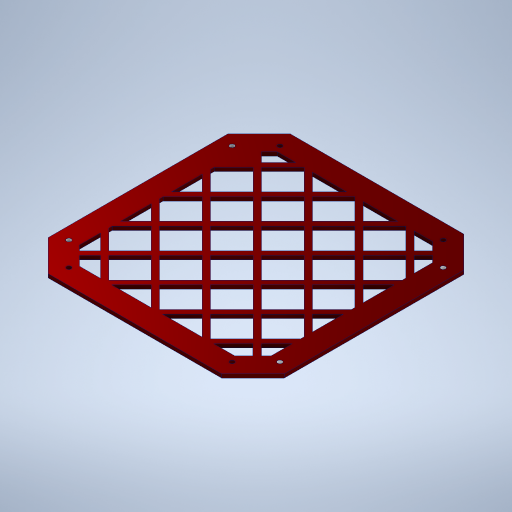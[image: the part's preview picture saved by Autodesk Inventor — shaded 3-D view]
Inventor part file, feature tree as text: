
AUTODESK INVENTOR PART (.ipt)
format: ipt  version: 2024.2 (Build 282272000, 272)  size: 547,328 bytes
history: native  units: in
note: dims shown in document units (in); Inventor stores cm internally (conversion verified against a paired STEP export)
features: extrude x4, sketch x4, chamfer x2, projected_geometry x2
ambient origin geometry x8: Origin, YZ Plane, XZ Plane, XY Plane, X Axis, Y Axis, Z Axis, Center Point
bodies: Body1 (feature_tree)
feature tree (12):
  extrude  "Extrusion4"  Depth=8.207in
  sketch  "Sketch5"  dims[d29=0.125in d30=0.0in d31=8.0in]
  extrude  "Extrusion7"  Depth=8.0in
  chamfer  "Chamfer1"  Distance=7.153in
  chamfer  "Chamfer2"  Distance=0.157in
  extrude  "Extrusion8"  Depth=1.25in
  extrude  "Extrusion9"  Depth=1.25in
  sketch  "Sketch4"  dims[d27=8.0in d28=8.207in]
  projected_geometry  "Projected Loop2"
  sketch  "Sketch8"  dims[d32=8.207in]
  projected_geometry  "Projected Loop5"
  sketch  "Sketch9"  dims[d33=5.533in d34=7.153in d39=0.157in d40=0.157in d41=0.157in d42=0.157in d43=1.0625in d44=0.0in d45=1.0625in d46=0.125in d47=45.0deg d48=1.0625in d49=0.125in d50=45.0deg d51=0.75in d52=0.5in d53=0.2in d54=2.7559in d56=1.22in d57=0.3937in d59=1.0in d61=0.375in d62=0.0in d63=7.153in d64=5.533in d65=7.153in d66=5.533in d67=0.157in d68=0.157in d69=0.157in d70=0.157in d71=1.25in d72=0.0in]
